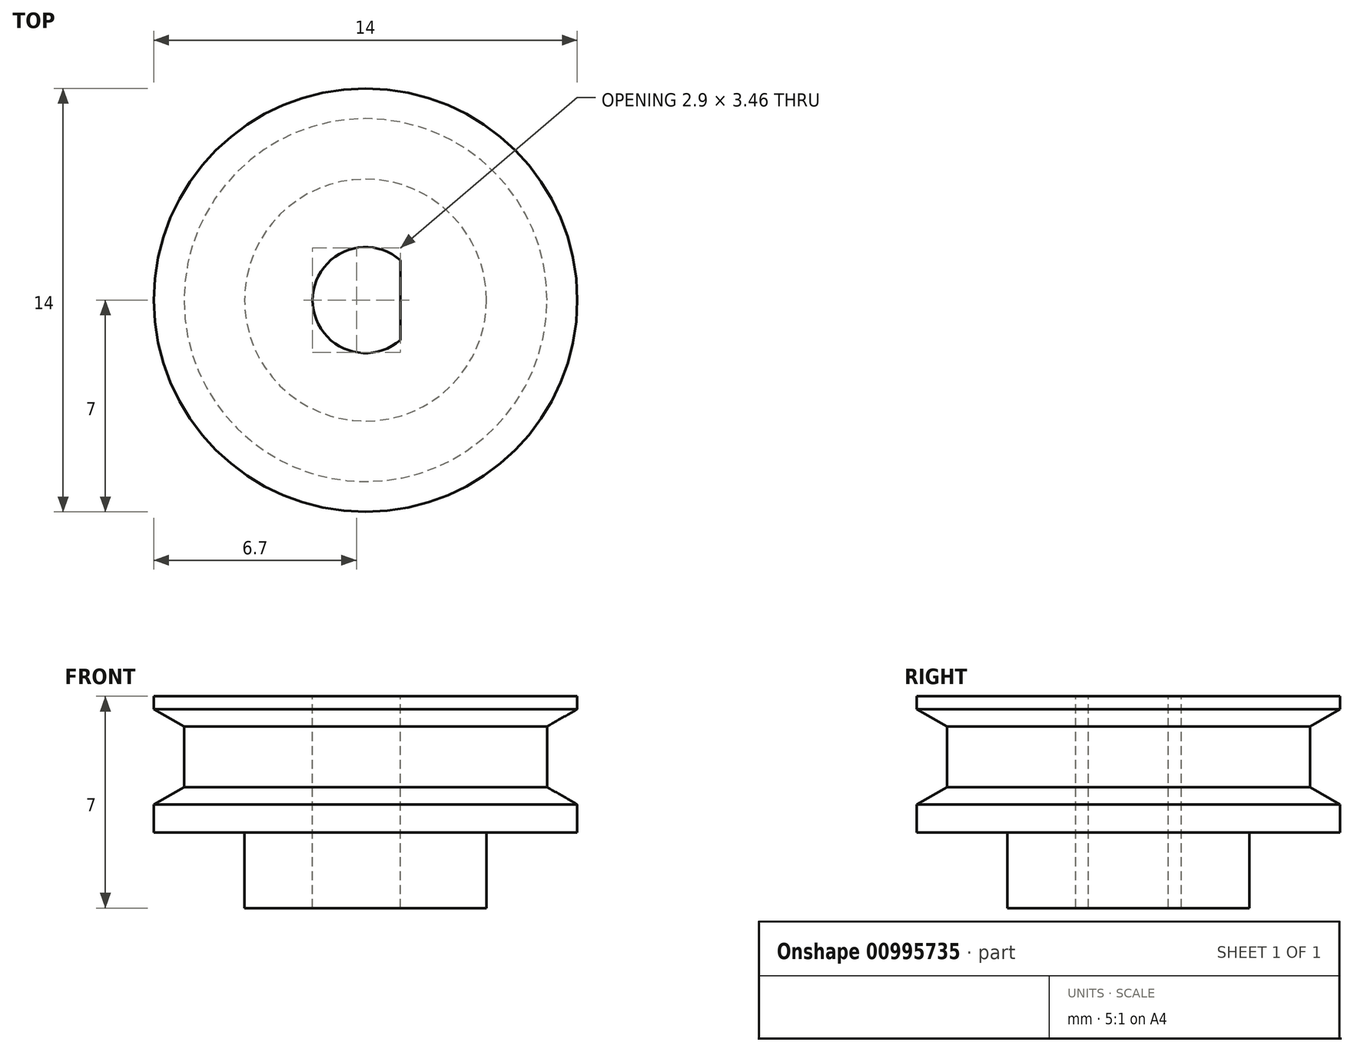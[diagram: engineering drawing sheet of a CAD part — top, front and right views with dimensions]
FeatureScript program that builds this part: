
annotation { "Feature Type Name" : "Feature", "Feature Type Description" : "" }
export const myFeature = defineFeature(function(context is Context, id is Id, definition is map)
    precondition{}
    {
        {
            var Q0;
            Q0=qCreatedBy(makeId("Front.planeOp"),FACE);
            var sketch = newSketch(context, id + "F0", { "sketchPlane" : qUnion([Q0])});
            skLineSegment(sketch, "E0", {"start": v(0, 0) * mm, "end": v(4, 0) * mm});
            skLineSegment(sketch, "E1", {"start": v(4, 0) * mm, "end": v(4, 2.5) * mm});
            skLineSegment(sketch, "E2", {"start": v(4, 2.5) * mm, "end": v(7, 2.5) * mm});
            skLineSegment(sketch, "E3", {"start": v(7, 2.5) * mm, "end": v(7, 7) * mm});
            skLineSegment(sketch, "E4", {"start": v(7, 7) * mm, "end": v(0, 7) * mm});
            skLineSegment(sketch, "E5", {"start": v(0, 7) * mm, "end": v(0, 0) * mm});
            skSolve(sketch);
        }
        {
            var Q0;
            Q0=makeQuery(id+"F0.imprint","IMPRINT",FACE,{"disambiguationData":[TD([[makeQuery(id+"F0.imprint","IMPRINT",EDGE,{"derivedFrom":sQuery(id+"F0.wireOp",EDGE,"E0")}),1.0]])]});
            var Q1;
            Q1=sQuery(id+"F0.wireOp",EDGE,"E5");
            revolve(context, id + "F1", {"surfaceOperationType" : NewSurfaceOperationType.NEW, "entities" : qUnion([Q0]), "axis" : qUnion([Q1]), "revolveType" : RevolveType.FULL});
        }
        {
            var Q0;
            Q0=makeQuery(id+"F1.opRevolve","SWEPT_FACE",FACE,{"disambiguationData":[OSD([sQuery(id+"F0.wireOp",EDGE,"E4")])]});
            var sketch = newSketch(context, id + "F2", { "sketchPlane" : qUnion([Q0])});
            skCircle(sketch, "E6", {"center": v(0, 0) * mm, "radius": 1.75 * mm});
            skLineSegment(sketch, "E7", {"start": v(1.15, 1.32) * mm, "end": v(1.15, -1.32) * mm});
            skSolve(sketch);
        }
        {
            var Q0;
            {var subQ0=sQuery(id+"F2.wireOp",EDGE,"E7");Q0=makeQuery(id+"F2.imprint","IMPRINT",FACE,{"disambiguationData":[TD([[makeQuery(id+"F2.imprint","IMPRINT",EDGE,{"derivedFrom":subQ0}),-1.0]])]});}
            extrude(context, id + "F3", {"entities" : qUnion([Q0]), "operationType" : NewBodyOperationType.REMOVE, "endBound" : BoundingType.THROUGH_ALL, "oppositeDirection" : true, "depth" : 25 * mm, "offsetDistance" : 25 * mm});
        }
        {
            var Q0;
            Q0=qCreatedBy(makeId("Front.planeOp"),FACE);
            var sketch = newSketch(context, id + "F4", { "sketchPlane" : qUnion([Q0])});
            skLineSegment(sketch, "E8", {"start": v(8.6, 2.5) * mm, "end": v(8.6, 7.5) * mm});
            skLineSegment(sketch, "E9", {"start": v(8.6, 7.5) * mm, "end": v(6, 6) * mm});
            skLineSegment(sketch, "E10", {"start": v(6, 6) * mm, "end": v(6, 4) * mm});
            skLineSegment(sketch, "E11", {"start": v(6, 4) * mm, "end": v(8.6, 2.5) * mm});
            skSolve(sketch);
        }
        {
            var Q0;
            Q0=makeQuery(id+"F4.imprint","IMPRINT",FACE,{"disambiguationData":[TD([[makeQuery(id+"F4.imprint","IMPRINT",EDGE,{"derivedFrom":sQuery(id+"F4.wireOp",EDGE,"E8")}),1.0]])]});
            var Q1;
            Q1=makeQuery(id+"F1.opRevolve","SWEPT_EDGE",EDGE,{"disambiguationData":[OSD([sQuery(id+"F0.wireOp",EDGE,"E3"),sQuery(id+"F0.wireOp",EDGE,"E4")])]});
            revolve(context, id + "F5", {"operationType" : NewBodyOperationType.REMOVE, "surfaceOperationType" : NewSurfaceOperationType.NEW, "entities" : qUnion([Q0]), "axis" : qUnion([Q1]), "revolveType" : RevolveType.FULL, "oppositeDirection" : true});
        }
    });
